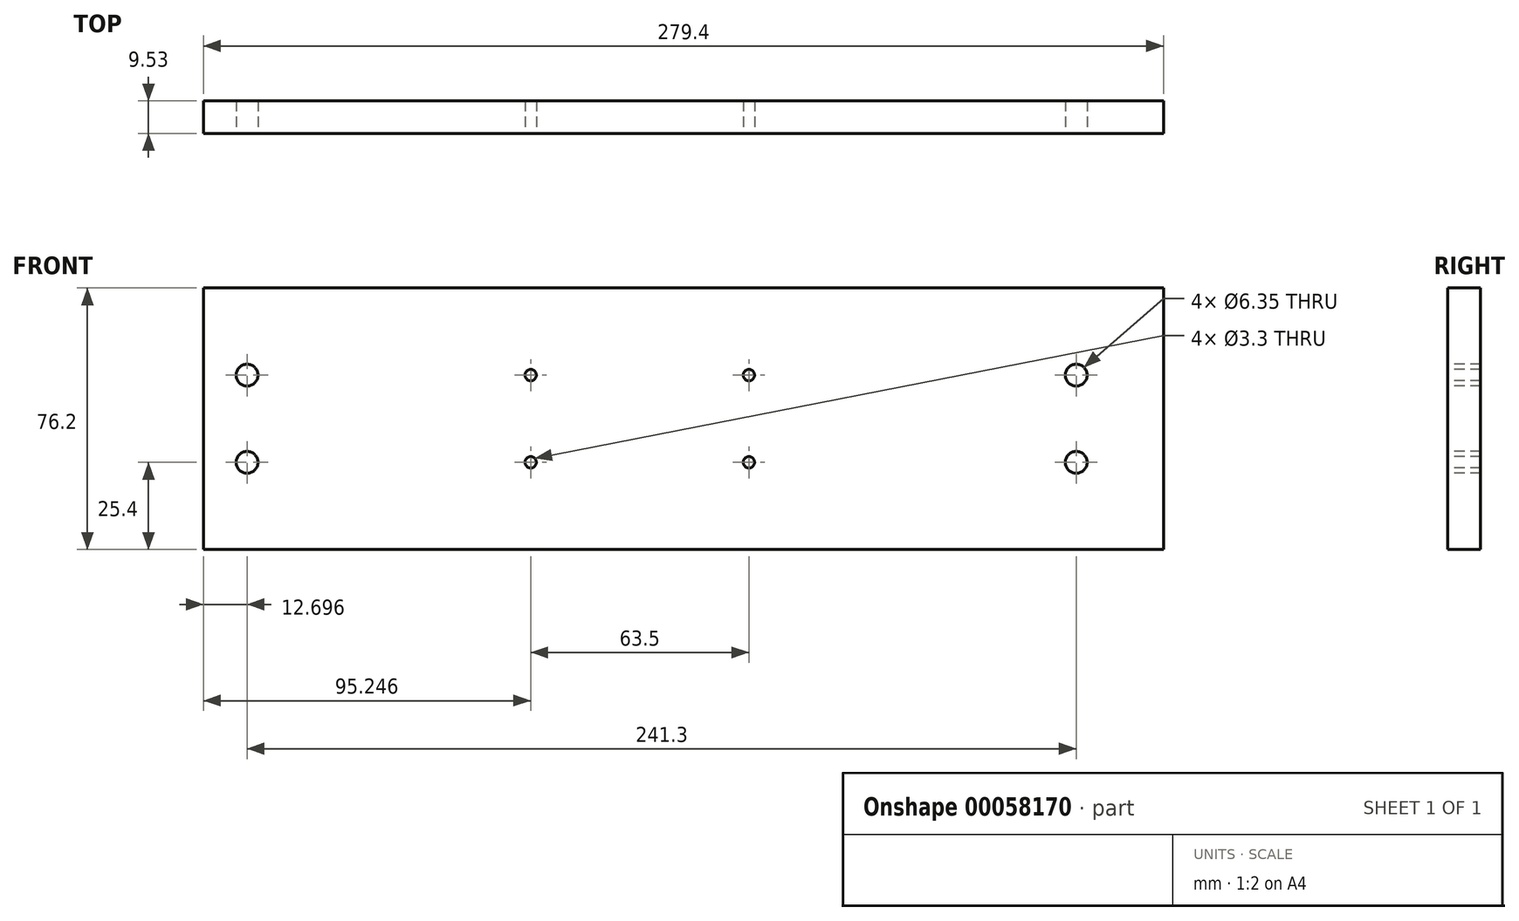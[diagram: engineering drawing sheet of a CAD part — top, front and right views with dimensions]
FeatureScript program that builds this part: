
annotation { "Feature Type Name" : "Feature", "Feature Type Description" : "" }
export const myFeature = defineFeature(function(context is Context, id is Id, definition is map)
    precondition{}
    {
        {
            var Q0;
            Q0=qCreatedBy(makeId("Front.planeOp"),FACE);
            var sketch = newSketch(context, id + "F0", { "sketchPlane" : qUnion([Q0])});
            skLineSegment(sketch, "E0", {"start": v(-91.15, -38.1) * mm, "end": v(188.25, -38.1) * mm});
            skLineSegment(sketch, "E1", {"start": v(188.25, -38.1) * mm, "end": v(188.25, 38.1) * mm});
            skLineSegment(sketch, "E2", {"start": v(188.25, 38.1) * mm, "end": v(-91.15, 38.1) * mm});
            skLineSegment(sketch, "E3", {"start": v(-91.15, 38.1) * mm, "end": v(-91.15, -38.1) * mm});
            skSolve(sketch);
        }
        {
            var Q0;
            Q0 = qSketchRegion(id + "F0", true);
            extrude(context, id + "F1", {"entities" : qUnion([Q0]), "depth" : 9.52 * mm});
        }
        {
            var Q0;
            Q0=makeQuery(id+"F1.opExtrude","CAP_FACE",FACE,{"disambiguationData":[OSD([sQuery(id+"F0.wireOp",EDGE,"E0"),sQuery(id+"F0.wireOp",EDGE,"E1"),sQuery(id+"F0.wireOp",EDGE,"E2"),sQuery(id+"F0.wireOp",EDGE,"E3")])],"isStart":false});
            var sketch = newSketch(context, id + "F2", { "sketchPlane" : qUnion([Q0])});
            skCircle(sketch, "E4", {"center": v(-78.45, -12.7) * mm, "radius": 3.18 * mm});
            skCircle(sketch, "E5", {"center": v(-78.45, 12.7) * mm, "radius": 3.18 * mm});
            skCircle(sketch, "E6", {"center": v(4.1, 12.7) * mm, "radius": 1.65 * mm});
            skCircle(sketch, "E7", {"center": v(4.1, -12.7) * mm, "radius": 1.65 * mm});
            skCircle(sketch, "E8", {"center": v(67.6, 12.7) * mm, "radius": 1.65 * mm});
            skCircle(sketch, "E9", {"center": v(67.6, -12.7) * mm, "radius": 1.65 * mm});
            skCircle(sketch, "E10", {"center": v(162.85, 12.7) * mm, "radius": 3.18 * mm});
            skCircle(sketch, "E11", {"center": v(162.85, -12.7) * mm, "radius": 3.18 * mm});
            skSolve(sketch);
        }
        {
            var Q0;
            Q0 = qSketchRegion(id + "F2", true);
            extrude(context, id + "F3", {"entities" : qUnion([Q0]), "operationType" : NewBodyOperationType.REMOVE, "endBound" : BoundingType.UP_TO_NEXT, "oppositeDirection" : true, "depth" : 25.4 * mm});
        }
    });
